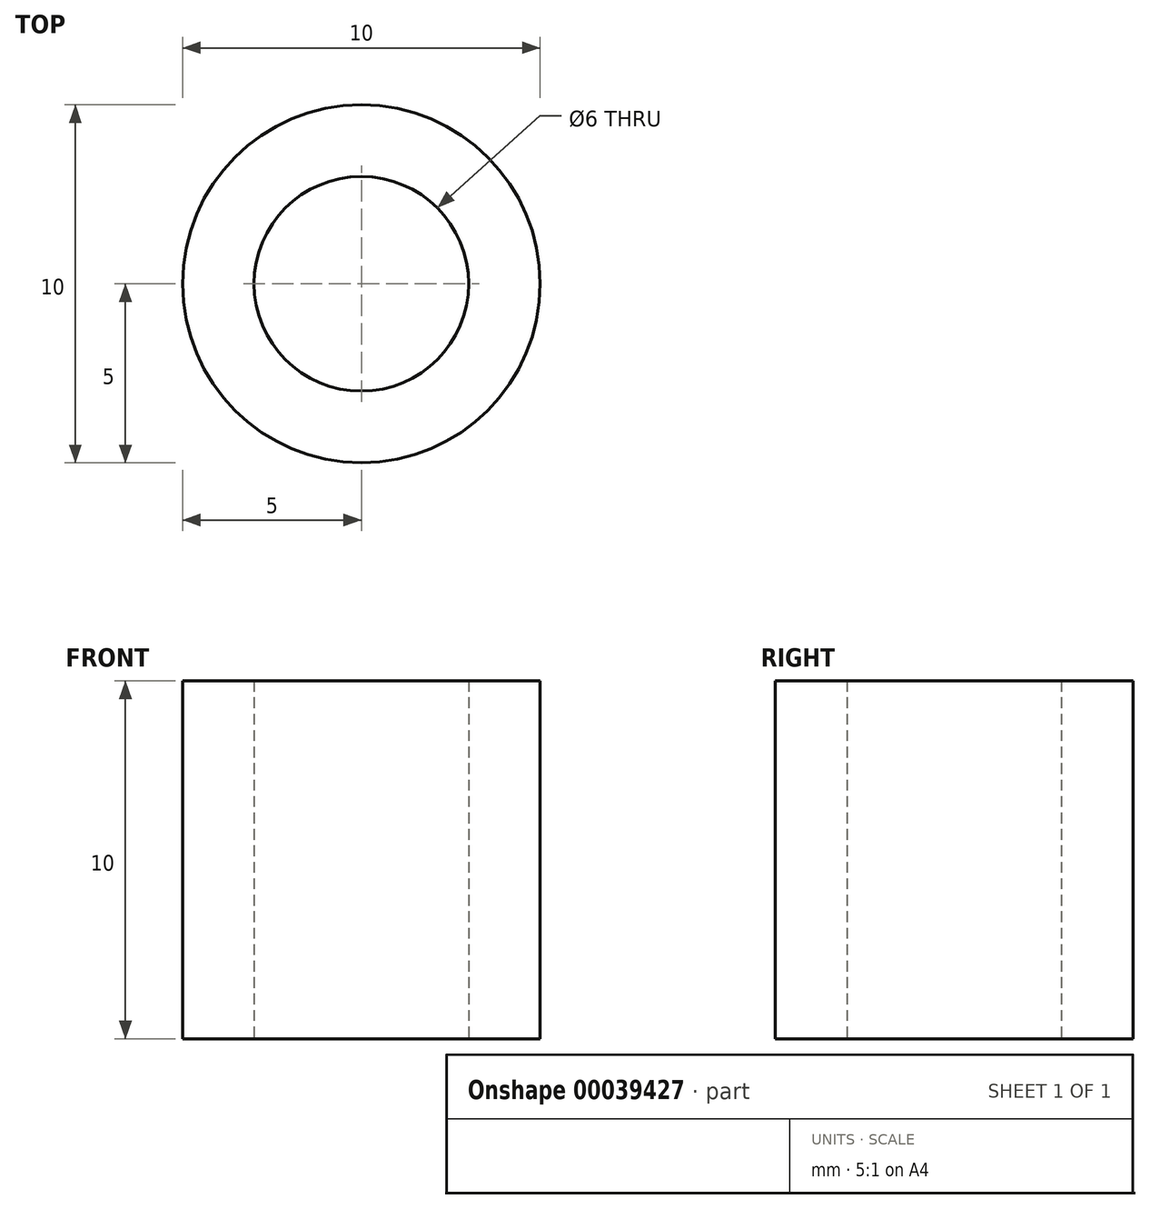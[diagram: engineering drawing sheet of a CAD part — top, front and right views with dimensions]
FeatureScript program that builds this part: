
annotation { "Feature Type Name" : "Feature", "Feature Type Description" : "" }
export const myFeature = defineFeature(function(context is Context, id is Id, definition is map)
    precondition{}
    {
        {
            var Q0;
            Q0=qCreatedBy(makeId("Top.planeOp"),FACE);
            var sketch = newSketch(context, id + "F0", { "sketchPlane" : qUnion([Q0])});
            skCircle(sketch, "E0", {"center": v(0, 0) * mm, "radius": 3 * mm});
            skCircle(sketch, "E1", {"center": v(0, 0) * mm, "radius": 5 * mm});
            skSolve(sketch);
        }
        {
            var Q0;
            Q0 = qSketchRegion(id + "F0", true);
            extrude(context, id + "F1", {"entities" : qUnion([Q0]), "depth" : 10 * mm});
        }
    });
